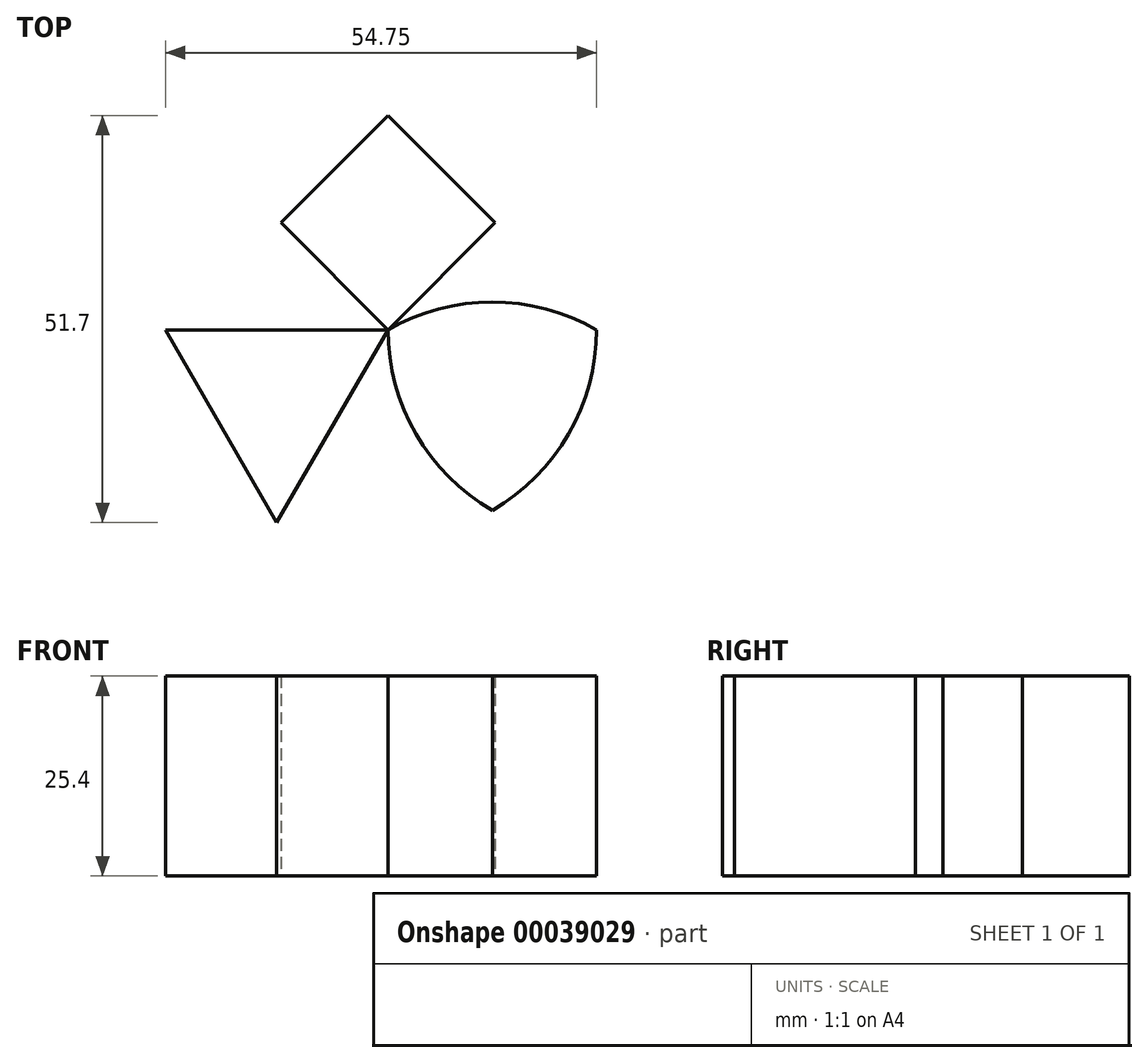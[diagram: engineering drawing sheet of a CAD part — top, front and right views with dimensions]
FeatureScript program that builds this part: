
annotation { "Feature Type Name" : "Feature", "Feature Type Description" : "" }
export const myFeature = defineFeature(function(context is Context, id is Id, definition is map)
    precondition{}
    {
        {
            var Q0;
            Q0=qCreatedBy(makeId("Top.planeOp"),FACE);
            var sketch = newSketch(context, id + "F0", { "sketchPlane" : qUnion([Q0])});
            skCircle(sketch, "E0.cCircle", {"center": v(0, 0) * mm, "radius": 28.27 * mm, "construction": true});
            skLineSegment(sketch, "E0.0", {"start": v(-28.27, 0) * mm, "end": v(-14.13, 24.48) * mm});
            skLineSegment(sketch, "E0.1", {"start": v(-14.13, 24.48) * mm, "end": v(14.13, 24.48) * mm});
            skLineSegment(sketch, "E0.2", {"start": v(14.13, 24.48) * mm, "end": v(28.27, 0) * mm});
            skLineSegment(sketch, "E0.3", {"start": v(28.27, 0) * mm, "end": v(14.13, -24.48) * mm});
            skLineSegment(sketch, "E0.4", {"start": v(14.13, -24.48) * mm, "end": v(-14.13, -24.48) * mm});
            skLineSegment(sketch, "E0.5", {"start": v(-14.13, -24.48) * mm, "end": v(-28.27, 0) * mm});
            skCircle(sketch, "E1.cCircle", {"center": v(-28.27, 0) * mm, "radius": 28.27 * mm, "construction": true});
            skLineSegment(sketch, "E1.0", {"start": v(0, 0) * mm, "end": v(-14.13, -24.48) * mm});
            skLineSegment(sketch, "E1.1", {"start": v(-14.13, -24.48) * mm, "end": v(-42.4, -24.48) * mm});
            skLineSegment(sketch, "E1.2", {"start": v(-42.4, -24.48) * mm, "end": v(-56.54, 0) * mm});
            skLineSegment(sketch, "E1.3", {"start": v(-56.54, 0) * mm, "end": v(-42.4, 24.48) * mm});
            skLineSegment(sketch, "E1.4", {"start": v(-42.4, 24.48) * mm, "end": v(-14.13, 24.48) * mm});
            skLineSegment(sketch, "E1.5", {"start": v(-14.13, 24.48) * mm, "end": v(0, 0) * mm});
            skCircle(sketch, "E2.cCircle", {"center": v(-14.13, -24.48) * mm, "radius": 28.27 * mm, "construction": true});
            skLineSegment(sketch, "E2.0", {"start": v(0, 0) * mm, "end": v(14.13, -24.48) * mm});
            skLineSegment(sketch, "E2.1", {"start": v(14.13, -24.48) * mm, "end": v(0, -48.96) * mm});
            skLineSegment(sketch, "E2.2", {"start": v(0, -48.96) * mm, "end": v(-28.27, -48.96) * mm});
            skLineSegment(sketch, "E2.3", {"start": v(-28.27, -48.96) * mm, "end": v(-42.4, -24.48) * mm});
            skLineSegment(sketch, "E2.4", {"start": v(-42.4, -24.48) * mm, "end": v(-28.27, 0) * mm});
            skLineSegment(sketch, "E2.5", {"start": v(-28.27, 0) * mm, "end": v(0, 0) * mm});
            skSolve(sketch);
        }
        {
            var Q0;
            Q0=makeQuery(id+"F0.imprint","IMPRINT",FACE,{"disambiguationData":[TD([[makeQuery(id+"F0.imprint","IMPRINT",EDGE,{"derivedFrom":sQuery(id+"F0.wireOp",EDGE,"E0.5")}),-1.0]])]});
            extrude(context, id + "F1", {"entities" : qUnion([Q0]), "depth" : 25.4 * mm});
        }
        {
            var Q0;
            Q0=qCreatedBy(makeId("Top.planeOp"),FACE);
            var sketch = newSketch(context, id + "F2", { "sketchPlane" : qUnion([Q0])});
            skCircle(sketch, "E3", {"center": v(0, 0) * mm, "radius": 26.48 * mm});
            skCircle(sketch, "E4", {"center": v(26.48, 0) * mm, "radius": 26.48 * mm});
            skCircle(sketch, "E5", {"center": v(13.24, -22.93) * mm, "radius": 26.48 * mm});
            skSolve(sketch);
        }
        {
            var Q0;
            {var subQ1=sQuery(id+"F2.wireOp",EDGE,"E5");var subQ3=sQuery(id+"F2.wireOp",EDGE,"E3");var subQ5=makeQuery(id+"F2.imprint","INTERSECT",VERTEX,{"disambiguationData":[OD(1.0)],"derivedFrom":[subQ3,subQ1]});Q0=makeQuery(id+"F2.imprint","IMPRINT",FACE,{"disambiguationData":[TD([[makeQuery(id+"F2.imprint","IMPRINT",EDGE,{"disambiguationData":[TD([[subQ5,1.0]])],"derivedFrom":subQ3}),1.0]])]});}
            extrude(context, id + "F3", {"entities" : qUnion([Q0]), "depth" : 25.4 * mm});
        }
        {
            var Q0;
            Q0=qCreatedBy(makeId("Top.planeOp"),FACE);
            var sketch = newSketch(context, id + "F4", { "sketchPlane" : qUnion([Q0])});
            skCircle(sketch, "E6.cCircle", {"center": v(0, 0) * mm, "radius": 27.22 * mm, "construction": true});
            skLineSegment(sketch, "E6.0", {"start": v(0, 27.22) * mm, "end": v(27.22, 0) * mm});
            skLineSegment(sketch, "E6.1", {"start": v(27.22, 0) * mm, "end": v(0, -27.22) * mm});
            skLineSegment(sketch, "E6.2", {"start": v(0, -27.22) * mm, "end": v(-27.22, 0) * mm});
            skLineSegment(sketch, "E6.3", {"start": v(-27.22, 0) * mm, "end": v(0, 27.22) * mm});
            skCircle(sketch, "E7.cCircle", {"center": v(0, 27.22) * mm, "radius": 27.22 * mm, "construction": true});
            skLineSegment(sketch, "E7.0", {"start": v(0, 0) * mm, "end": v(-27.22, 27.22) * mm});
            skLineSegment(sketch, "E7.1", {"start": v(-27.22, 27.22) * mm, "end": v(0, 54.44) * mm});
            skLineSegment(sketch, "E7.2", {"start": v(0, 54.44) * mm, "end": v(27.22, 27.22) * mm});
            skLineSegment(sketch, "E7.3", {"start": v(27.22, 27.22) * mm, "end": v(0, 0) * mm});
            skSolve(sketch);
        }
        {
            var Q0;
            {var subQ1=sQuery(id+"F4.wireOp",EDGE,"E6.0");var subQ5=sQuery(id+"F4.wireOp",EDGE,"E6.3");var subQ7=makeQuery(id+"F4.imprint","INTERSECT",VERTEX,{"derivedFrom":[subQ1,subQ5]});Q0=makeQuery(id+"F4.imprint","IMPRINT",FACE,{"disambiguationData":[TD([[makeQuery(id+"F4.imprint","IMPRINT",EDGE,{"disambiguationData":[TD([[subQ7,-1.0]])],"derivedFrom":subQ1}),-1.0]])]});}
            extrude(context, id + "F5", {"entities" : qUnion([Q0]), "depth" : 25.4 * mm});
        }
    });
